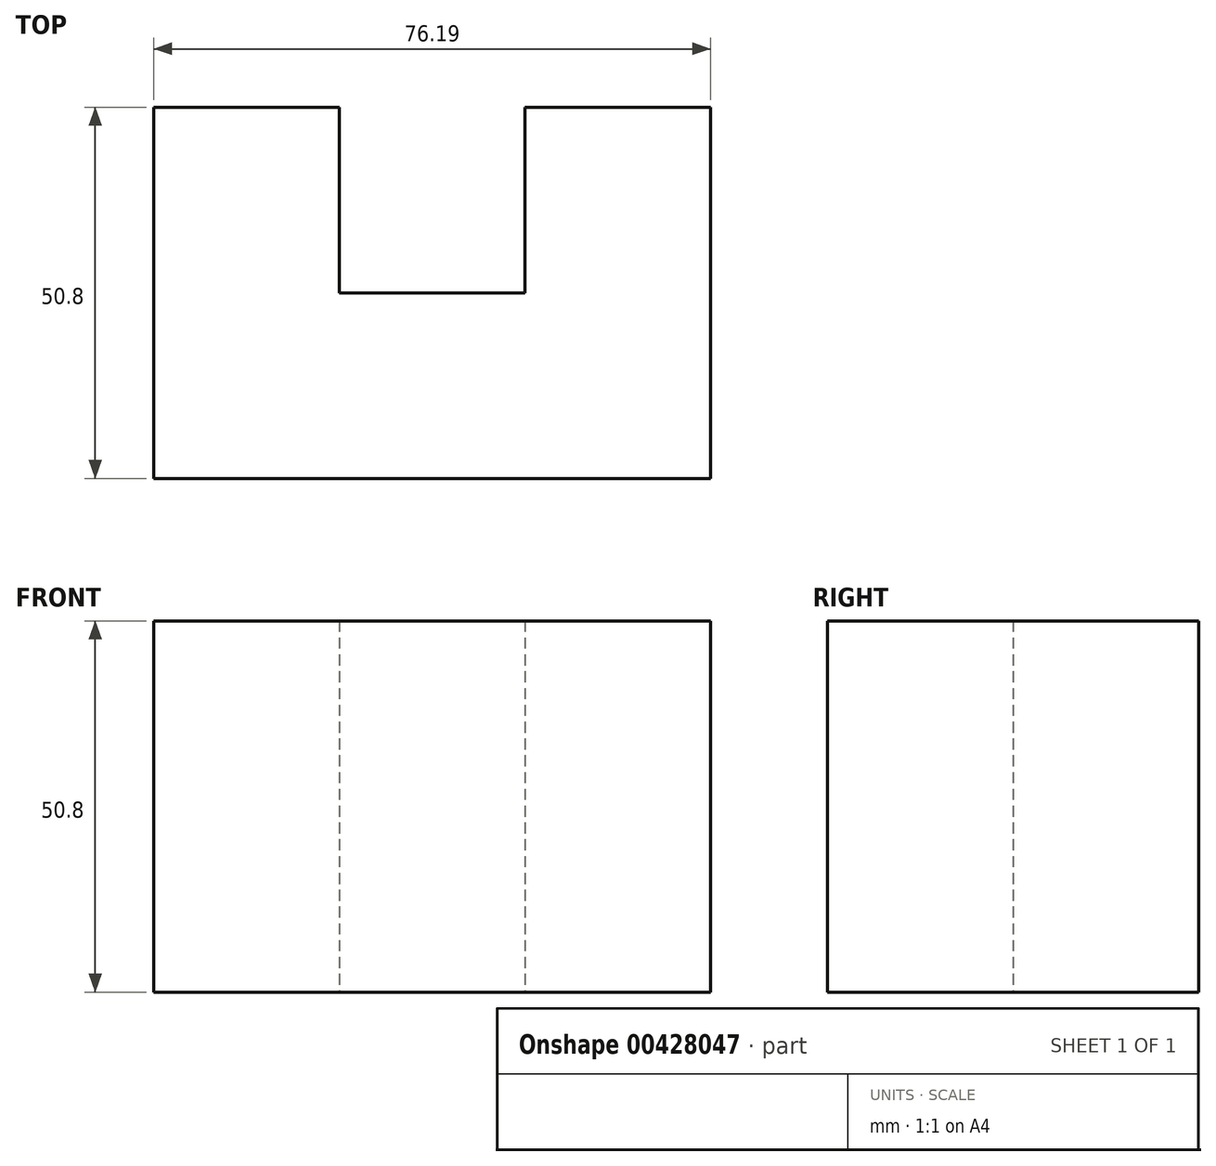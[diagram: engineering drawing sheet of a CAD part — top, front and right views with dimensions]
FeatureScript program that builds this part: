
annotation { "Feature Type Name" : "Feature", "Feature Type Description" : "" }
export const myFeature = defineFeature(function(context is Context, id is Id, definition is map)
    precondition{}
    {
        {
            var Q0;
            Q0=qCreatedBy(makeId("Top.planeOp"),FACE);
            var sketch = newSketch(context, id + "F0", { "sketchPlane" : qUnion([Q0])});
            skLineSegment(sketch, "E0", {"start": v(0, 0) * mm, "end": v(0, 50.8) * mm});
            skLineSegment(sketch, "E1", {"start": v(0, 50.8) * mm, "end": v(25.4, 50.8) * mm});
            skLineSegment(sketch, "E2", {"start": v(25.4, 50.8) * mm, "end": v(25.4, 25.4) * mm});
            skLineSegment(sketch, "E3", {"start": v(25.4, 25.4) * mm, "end": v(50.8, 25.4) * mm});
            skLineSegment(sketch, "E4", {"start": v(50.8, 25.4) * mm, "end": v(50.8, 50.8) * mm});
            skLineSegment(sketch, "E5", {"start": v(50.8, 50.8) * mm, "end": v(76.19, 50.8) * mm});
            skLineSegment(sketch, "E6", {"start": v(76.19, 50.8) * mm, "end": v(76.19, 0) * mm});
            skLineSegment(sketch, "E7", {"start": v(76.19, 0) * mm, "end": v(0, 0) * mm});
            skSolve(sketch);
        }
        {
            var Q0;
            Q0=makeQuery(id+"F0.imprint","IMPRINT",FACE,{"disambiguationData":[TD([[makeQuery(id+"F0.imprint","IMPRINT",EDGE,{"derivedFrom":sQuery(id+"F0.wireOp",EDGE,"E0")}),-1.0]])]});
            extrude(context, id + "F1", {"entities" : qUnion([Q0]), "depth" : 50.8 * mm});
        }
    });
